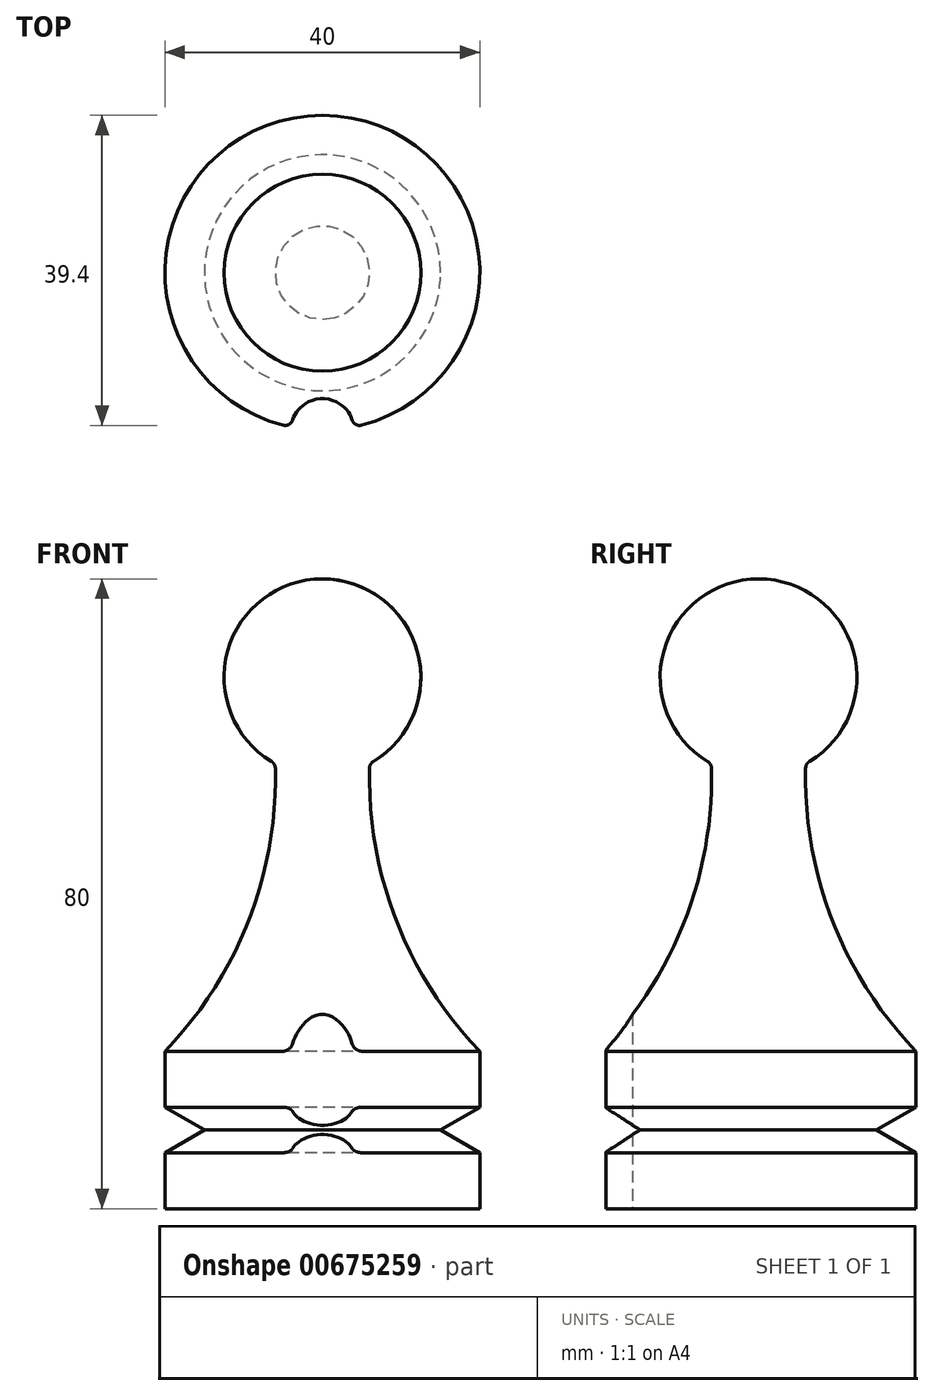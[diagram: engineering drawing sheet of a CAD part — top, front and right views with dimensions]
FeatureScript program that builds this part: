
annotation { "Feature Type Name" : "Feature", "Feature Type Description" : "" }
export const myFeature = defineFeature(function(context is Context, id is Id, definition is map)
    precondition{}
    {
        {
            var Q0;
            Q0=qCreatedBy(makeId("Front.planeOp"),FACE);
            var sketch = newSketch(context, id + "F0", { "sketchPlane" : qUnion([Q0])});
            skLineSegment(sketch, "E0", {"start": v(0, 88.73) * mm, "end": v(0, -90.48) * mm, "construction": true});
            skLineSegment(sketch, "E1", {"start": v(0, 0) * mm, "end": v(20, 0) * mm});
            skLineSegment(sketch, "E2", {"start": v(20, 7.11) * mm, "end": v(20, 0) * mm});
            skLineSegment(sketch, "E3", {"start": v(20, 7.11) * mm, "end": v(15, 10) * mm});
            skLineSegment(sketch, "E4", {"start": v(15, 10) * mm, "end": v(20, 12.89) * mm});
            skLineSegment(sketch, "E5", {"start": v(20, 12.89) * mm, "end": v(20, 20) * mm});
            skArc(sketch, "E6", {"start": v(6, 56.53) * mm, "mid": v(9.28, 36.84) * mm, "end": v(20, 20) * mm});
            skArc(sketch, "E7", {"start": v(6, 56.53) * mm, "mid": v(12.11, 70.6) * mm, "end": v(0, 80) * mm});
            skLineSegment(sketch, "E8", {"start": v(0, 80) * mm, "end": v(0, 0) * mm});
            skSolve(sketch);
        }
        {
            var Q0;
            Q0=makeQuery(id+"F0.imprint","IMPRINT",FACE,{"disambiguationData":[TD([[makeQuery(id+"F0.imprint","IMPRINT",EDGE,{"derivedFrom":sQuery(id+"F0.wireOp",EDGE,"E1")}),1.0]])]});
            var Q1;
            Q1=sQuery(id+"F0.wireOp",EDGE,"E0");
            revolve(context, id + "F1", {"entities" : qUnion([Q0]), "axis" : qUnion([Q1]), "revolveType" : RevolveType.FULL});
        }
        {
            var Q0;
            Q0=makeQuery(id+"F1.opRevolve","SWEPT_FACE",FACE,{"disambiguationData":[OSD([sQuery(id+"F0.wireOp",EDGE,"E1")])]});
            var sketch = newSketch(context, id + "F2", { "sketchPlane" : qUnion([Q0])});
            skCircle(sketch, "E9", {"center": v(0, 20) * mm, "radius": 4 * mm});
            skSolve(sketch);
        }
        {
            var Q0;
            Q0 = qSketchRegion(id + "F2", true);
            extrude(context, id + "F3", {"entities" : qUnion([Q0]), "operationType" : NewBodyOperationType.REMOVE, "oppositeDirection" : true, "depth" : 42 * mm, "offsetDistance" : 25 * mm});
        }
        {
            var Q0;
            Q0=makeQuery(id+"F3.boolean.opBoolean","INTERSECT",EDGE,{"disambiguationData":[OD(0.0)],"derivedFrom":[makeQuery(id+"F1.opRevolve","SWEPT_FACE",FACE,{"disambiguationData":[OSD([sQuery(id+"F0.wireOp",EDGE,"E5")])]}),makeQuery(id+"F3.opExtrude","SWEPT_FACE",FACE,{"disambiguationData":[OSD([sQuery(id+"F2.wireOp",EDGE,"E9")])]})]});
            var Q1;
            Q1=makeQuery(id+"F3.boolean.opBoolean","INTERSECT",EDGE,{"disambiguationData":[OD(1.0)],"derivedFrom":[makeQuery(id+"F1.opRevolve","SWEPT_FACE",FACE,{"disambiguationData":[OSD([sQuery(id+"F0.wireOp",EDGE,"E5")])]}),makeQuery(id+"F3.opExtrude","SWEPT_FACE",FACE,{"disambiguationData":[OSD([sQuery(id+"F2.wireOp",EDGE,"E9")])]})]});
            var Q2;
            Q2=makeQuery(id+"F3.boolean.opBoolean","INTERSECT",EDGE,{"disambiguationData":[OD(0.0)],"derivedFrom":[makeQuery(id+"F1.opRevolve","SWEPT_FACE",FACE,{"disambiguationData":[OSD([sQuery(id+"F0.wireOp",EDGE,"E2")])]}),makeQuery(id+"F3.opExtrude","SWEPT_FACE",FACE,{"disambiguationData":[OSD([sQuery(id+"F2.wireOp",EDGE,"E9")])]})]});
            var Q3;
            Q3=makeQuery(id+"F3.boolean.opBoolean","INTERSECT",EDGE,{"disambiguationData":[OD(1.0)],"derivedFrom":[makeQuery(id+"F1.opRevolve","SWEPT_FACE",FACE,{"disambiguationData":[OSD([sQuery(id+"F0.wireOp",EDGE,"E2")])]}),makeQuery(id+"F3.opExtrude","SWEPT_FACE",FACE,{"disambiguationData":[OSD([sQuery(id+"F2.wireOp",EDGE,"E9")])]})]});
            fillet(context, id + "F4", {"entities" : qUnion([Q0, Q1, Q2, Q3]), "radius" : 1 * mm, "tangentPropagation" : true, "allowEdgeOverflow" : false});
        }
        {
            var Q0;
            Q0=makeQuery(id+"F1.opRevolve","SWEPT_EDGE",EDGE,{"disambiguationData":[OSD([sQuery(id+"F0.wireOp",EDGE,"E6"),sQuery(id+"F0.wireOp",EDGE,"E7")])]});
            fillet(context, id + "F5", {"entities" : qUnion([Q0]), "radius" : 1 * mm, "tangentPropagation" : true, "allowEdgeOverflow" : false});
        }
    });
